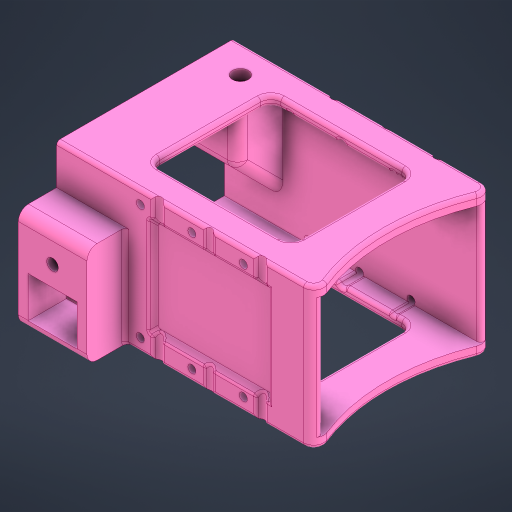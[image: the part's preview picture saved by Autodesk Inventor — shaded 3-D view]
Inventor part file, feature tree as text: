
AUTODESK INVENTOR PART (.ipt)
format: ipt  version: 2023.4 (Build 274418000, 418)  size: 995,328 bytes
history: native  units: mm
features: extrude x8, sketch x5, fillet x3, reference x3, projected_geometry x3, other x3, plane x2, mirror x1
ambient origin geometry x8: Origin, YZ Plane, XZ Plane, XY Plane, X Axis, Y Axis, Z Axis, Center Point
bodies: Solid1 (feature_tree)
feature tree (28):
  plane  "Work Plane2"
  extrude  "Extrusion1"  Depth=2.5mm
  sketch  "Sketch2"  dims[d2=0.375mm d3=0.375mm]
  extrude  "Extrusion2"  Depth=0.375mm
  extrude  "Extrusion3"  Depth=0.125mm
  extrude  "Extrusion4"  Depth=2.25mm
  plane  "Work Plane3"
  extrude  "Extrusion5"  Depth=10.0mm
  sketch  "Sketch5"  dims[d9=2.5mm d10=50.0mm d11=35.0mm d12=0.0mm d14=35.0mm d15=0.0mm d16=13.75mm d17=45.0deg d18=5.0mm d19=14.5mm d20=0.0mm d21=4.0mm d22=14.5mm d23=0.0mm d25=-2.5mm d27=8.375mm d28=0.0mm d31=17.0mm d32=15.0mm d33=2.425mm d34=5.0mm d35=9.5mm d36=0.0mm d37=9.9675mm d38=0.0mm d42=1.25mm d43=2.0mm d44=45.0deg d45=2.5mm d46=0.875mm d47=3.75mm d48=0.75mm d49=2.0mm d51=2.0mm d52=10.0mm d53=0.0mm d54=2.25mm d55=2.0mm d56=25.5mm d57=0.375mm d59=0.375mm d60=22.5mm d61=1.25mm d62=0.0mm d63=25.5mm d64=2.5mm d65=0.25mm d66=6.0mm d67=0.875mm d68=10.0mm d69=2.45mm d70=2.875mm d71=4.275mm d72=35.0mm d73=30.0mm d74=0.872665mm]
  extrude  "Extrusion7"  Depth=10.0mm TaperAngle=0.0deg
  extrude  "Extrusion8"  Depth=10.0mm TaperAngle=0.0deg
  extrude  "Extrusion9"  Depth=10.0mm
  mirror  "Mirror1"
  fillet  "Fillet1"  [1 undecoded]
  fillet  "Fillet2"  Radius=5.0mm
  fillet  "Fillet3"  Radius=14.5mm
  sketch  "Sketch1"  dims[d0=62.5mm d1=2.5mm]
  reference  "Reference2"
  projected_geometry  "Projected Loop1"
  sketch  "Sketch3"  dims[d4=7.5mm d5=0.125mm]
  reference  "Reference3"
  sketch  "Sketch4"  dims[d6=2.25mm d8=2.25mm]
  projected_geometry  "Projected Loop2"
  projected_geometry  "Projected Loop3"
  reference  "Reference4"
  parser-record x1  (decoder bookkeeping rows leaked as tree rows — omitted from the tree; the rows remain in map.json)
  other  "XYZ Stage V5.iam"
  other  "Z Stage Body V5:1"
note: 1 required parameter value undecoded (feature->parameter linkage not recoverable at this tier; creation-order binding heuristic only, values carry confidence <= 0.55)
note: 1 file-system path scrubbed to <path> (originals preserved in map.json)
